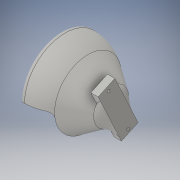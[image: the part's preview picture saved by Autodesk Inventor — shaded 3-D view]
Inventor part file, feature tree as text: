
AUTODESK INVENTOR PART (.ipt)
format: ipt  version: 2016 (Build 200138000, 138)  size: 1,047,552 bytes
history: native  units: in
note: dims shown in document units (in); Inventor stores cm internally (conversion verified against a paired STEP export)
features: fillet x4, sketch x3, revolve x2, hole x2, other x2, extrude x1, loft x1, projected_geometry x1
ambient origin geometry x8: Origin, YZ Plane, XZ Plane, XY Plane, X Axis, Y Axis, Z Axis, Center Point
bodies: Body1 (feature_tree)
feature tree (16):
  revolve  "Revolution2"  [1 undecoded]
  extrude  "Extrusion1"  Depth=1.0in
  loft  "Loft1"
  hole  "Hole7"  [1 undecoded]
  hole  "Hole8"  [1 undecoded]
  revolve  "Revolution3"  [1 undecoded]
  fillet  "Fillet2"  Radius=0.381in
  fillet  "Fillet3"  Radius=0.197in
  fillet  "Fillet4"  Radius=0.125in
  fillet  "Fillet10"  Radius=0.3in
  sketch  "Sketch3"  dims[d59=1.95in d60=2.2in]
  sketch  "Sketch5"  dims[d62=90.0deg d64=1.0in]
  projected_geometry  "Projected Loop1"
  other  "Edges1"
  other  "Edges2"
  sketch  "Sketch9"  dims[d65=3.0in d66=0.4in d67=0.0in d68=0.0in d69=90.0deg d70=0.0in d71=90.0deg d124=1.0in d125=1.0in d96=0.1575in d97=0.75in d98=0.375in d99=0.25in d100=0.5635in d101=0.4in d102=0.8108in d122=1.0in d123=1.0in d105=0.1575in d106=0.75in d107=0.375in d108=0.25in d109=0.5635in d110=0.4in d111=0.8108in d112=1.4773in d113=0.381in d114=0.197in d115=0.125in d121=0.3in]
note: 4 required parameter values undecoded (feature->parameter linkage not recoverable at this tier; creation-order binding heuristic only, values carry confidence <= 0.55)